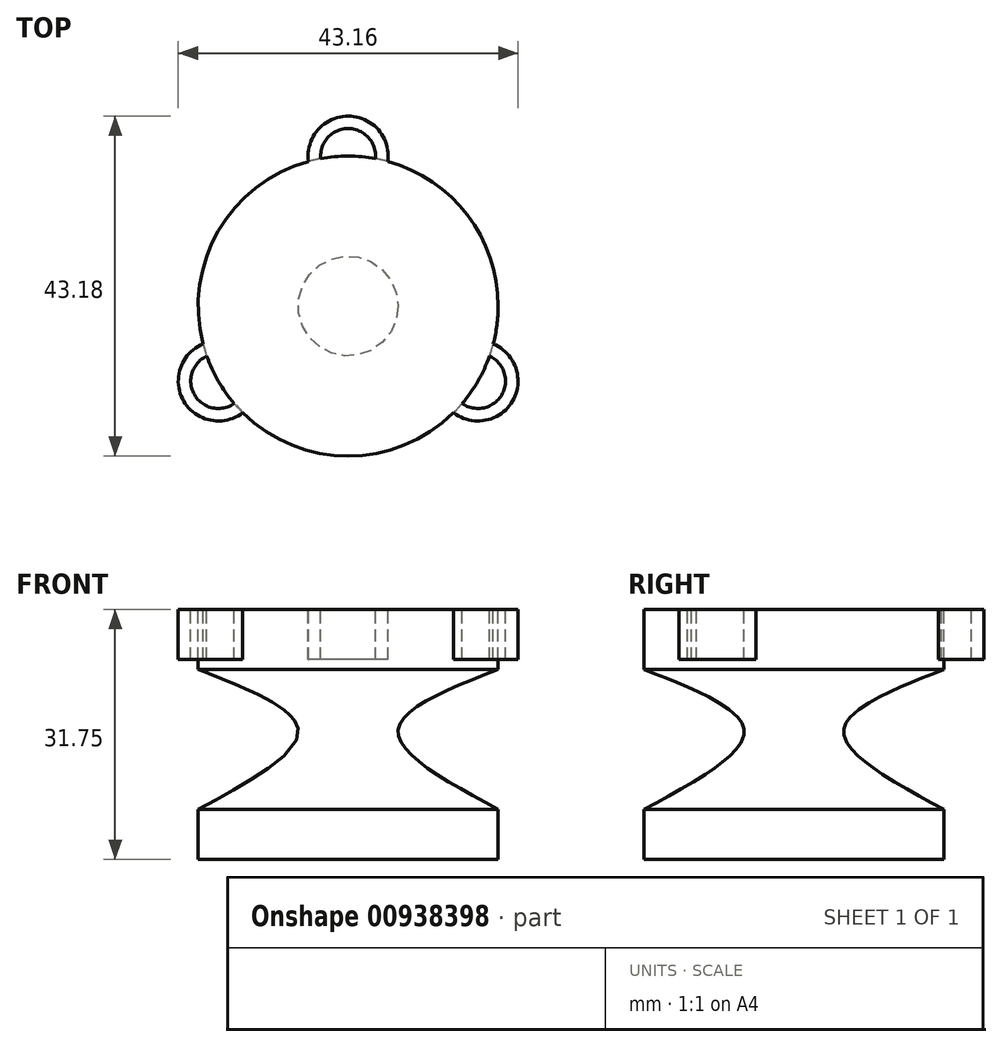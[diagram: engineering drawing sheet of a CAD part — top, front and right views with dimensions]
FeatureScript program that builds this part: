
annotation { "Feature Type Name" : "Feature", "Feature Type Description" : "" }
export const myFeature = defineFeature(function(context is Context, id is Id, definition is map)
    precondition{}
    {
        {
            var Q0;
            Q0=qCreatedBy(makeId("Top.planeOp"),FACE);
            var sketch = newSketch(context, id + "F0", { "sketchPlane" : qUnion([Q0])});
            skCircle(sketch, "E0", {"center": v(0, 0) * mm, "radius": 19.05 * mm});
            skCircle(sketch, "E1", {"center": v(0, 19.05) * mm, "radius": 5.08 * mm});
            skCircle(sketch, "E2.1.0", {"center": v(-16.5, -9.52) * mm, "radius": 5.08 * mm});
            skCircle(sketch, "E2.2.0", {"center": v(16.5, -9.53) * mm, "radius": 5.08 * mm});
            skCircle(sketch, "E3", {"center": v(0, 19.05) * mm, "radius": 3.5 * mm});
            skCircle(sketch, "E4.1.0", {"center": v(-16.5, -9.52) * mm, "radius": 3.5 * mm});
            skCircle(sketch, "E4.2.0", {"center": v(16.5, -9.53) * mm, "radius": 3.5 * mm});
            skSolve(sketch);
        }
        {
            var Q0;
            {var subQ0=sQuery(id+"F0.wireOp",EDGE,"E1");var subQ1=sQuery(id+"F0.wireOp",EDGE,"E0");var subQ8=makeQuery(id+"F0.imprint","INTERSECT",VERTEX,{"disambiguationData":[OD(0.0)],"derivedFrom":[subQ1,subQ0]});Q0=makeQuery(id+"F0.imprint","IMPRINT",FACE,{"disambiguationData":[TD([[makeQuery(id+"F0.imprint","IMPRINT",EDGE,{"disambiguationData":[TD([[subQ8,-1.0]])],"derivedFrom":subQ1}),1.0]])]});}
            var Q1;
            {var subQ0=sQuery(id+"F0.wireOp",EDGE,"E2.1.0");var subQ1=sQuery(id+"F0.wireOp",EDGE,"E0");var subQ2=makeQuery(id+"F0.imprint","INTERSECT",VERTEX,{"disambiguationData":[OD(0.0)],"derivedFrom":[subQ1,subQ0]});Q1=makeQuery(id+"F0.imprint","IMPRINT",FACE,{"disambiguationData":[TD([[makeQuery(id+"F0.imprint","IMPRINT",EDGE,{"disambiguationData":[TD([[subQ2,-1.0]])],"derivedFrom":subQ1}),1.0]])]});}
            var Q2;
            {var subQ0=sQuery(id+"F0.wireOp",EDGE,"E2.2.0");var subQ1=sQuery(id+"F0.wireOp",EDGE,"E0");var subQ2=makeQuery(id+"F0.imprint","INTERSECT",VERTEX,{"disambiguationData":[OD(0.0)],"derivedFrom":[subQ1,subQ0]});Q2=makeQuery(id+"F0.imprint","IMPRINT",FACE,{"disambiguationData":[TD([[makeQuery(id+"F0.imprint","IMPRINT",EDGE,{"disambiguationData":[TD([[subQ2,-1.0]])],"derivedFrom":subQ1}),1.0]])]});}
            var Q3;
            {var subQ0=sQuery(id+"F0.wireOp",EDGE,"E1");var subQ1=sQuery(id+"F0.wireOp",EDGE,"E0");var subQ2=makeQuery(id+"F0.imprint","INTERSECT",VERTEX,{"disambiguationData":[OD(0.0)],"derivedFrom":[subQ1,subQ0]});Q3=makeQuery(id+"F0.imprint","IMPRINT",FACE,{"disambiguationData":[TD([[makeQuery(id+"F0.imprint","IMPRINT",EDGE,{"disambiguationData":[TD([[subQ2,1.0]])],"derivedFrom":subQ1}),1.0]])]});}
            var Q4;
            {var subQ0=sQuery(id+"F0.wireOp",EDGE,"E3");var subQ1=sQuery(id+"F0.wireOp",EDGE,"E0");var subQ2=makeQuery(id+"F0.imprint","INTERSECT",VERTEX,{"disambiguationData":[OD(0.0)],"derivedFrom":[subQ1,subQ0]});Q4=makeQuery(id+"F0.imprint","IMPRINT",FACE,{"disambiguationData":[TD([[makeQuery(id+"F0.imprint","IMPRINT",EDGE,{"disambiguationData":[TD([[subQ2,-1.0]])],"derivedFrom":subQ1}),1.0]])]});}
            var Q5;
            {var subQ0=sQuery(id+"F0.wireOp",EDGE,"E4.1.0");var subQ1=sQuery(id+"F0.wireOp",EDGE,"E0");var subQ2=makeQuery(id+"F0.imprint","INTERSECT",VERTEX,{"disambiguationData":[OD(0.0)],"derivedFrom":[subQ1,subQ0]});Q5=makeQuery(id+"F0.imprint","IMPRINT",FACE,{"disambiguationData":[TD([[makeQuery(id+"F0.imprint","IMPRINT",EDGE,{"disambiguationData":[TD([[subQ2,-1.0]])],"derivedFrom":subQ1}),1.0]])]});}
            var Q6;
            {var subQ0=sQuery(id+"F0.wireOp",EDGE,"E4.2.0");var subQ1=sQuery(id+"F0.wireOp",EDGE,"E0");var subQ2=makeQuery(id+"F0.imprint","INTERSECT",VERTEX,{"disambiguationData":[OD(0.0)],"derivedFrom":[subQ1,subQ0]});Q6=makeQuery(id+"F0.imprint","IMPRINT",FACE,{"disambiguationData":[TD([[makeQuery(id+"F0.imprint","IMPRINT",EDGE,{"disambiguationData":[TD([[subQ2,-1.0]])],"derivedFrom":subQ1}),1.0]])]});}
            extrude(context, id + "F1", {"entities" : qUnion([Q0, Q1, Q2, Q3, Q4, Q5, Q6]), "oppositeDirection" : true, "depth" : 7.62 * mm, "offsetDistance" : 25.4 * mm});
        }
        {
            var Q0;
            {var subQ0=sQuery(id+"F0.wireOp",EDGE,"E1");var subQ1=sQuery(id+"F0.wireOp",EDGE,"E0");var subQ2=makeQuery(id+"F0.imprint","INTERSECT",VERTEX,{"disambiguationData":[OD(0.0)],"derivedFrom":[subQ1,subQ0]});Q0=makeQuery(id+"F0.imprint","IMPRINT",FACE,{"disambiguationData":[TD([[makeQuery(id+"F0.imprint","IMPRINT",EDGE,{"disambiguationData":[TD([[subQ2,-1.0]])],"derivedFrom":subQ1}),-1.0]])]});}
            var Q1;
            {var subQ0=sQuery(id+"F0.wireOp",EDGE,"E2.1.0");var subQ1=sQuery(id+"F0.wireOp",EDGE,"E0");var subQ2=makeQuery(id+"F0.imprint","INTERSECT",VERTEX,{"disambiguationData":[OD(0.0)],"derivedFrom":[subQ1,subQ0]});Q1=makeQuery(id+"F0.imprint","IMPRINT",FACE,{"disambiguationData":[TD([[makeQuery(id+"F0.imprint","IMPRINT",EDGE,{"disambiguationData":[TD([[subQ2,-1.0]])],"derivedFrom":subQ1}),-1.0]])]});}
            var Q2;
            {var subQ0=sQuery(id+"F0.wireOp",EDGE,"E2.2.0");var subQ1=sQuery(id+"F0.wireOp",EDGE,"E0");var subQ2=makeQuery(id+"F0.imprint","INTERSECT",VERTEX,{"disambiguationData":[OD(0.0)],"derivedFrom":[subQ1,subQ0]});Q2=makeQuery(id+"F0.imprint","IMPRINT",FACE,{"disambiguationData":[TD([[makeQuery(id+"F0.imprint","IMPRINT",EDGE,{"disambiguationData":[TD([[subQ2,-1.0]])],"derivedFrom":subQ1}),-1.0]])]});}
            extrude(context, id + "F2", {"entities" : qUnion([Q0, Q1, Q2]), "operationType" : NewBodyOperationType.ADD, "oppositeDirection" : true, "depth" : 6.35 * mm, "offsetDistance" : 25.4 * mm});
        }
        {
            var Q0;
            Q0=makeQuery(id+"F1.opExtrude","CAP_FACE",FACE,{"disambiguationData":[OSD([sQuery(id+"F0.wireOp",EDGE,"E0")])],"isStart":false});
            var sketch = newSketch(context, id + "F3", { "sketchPlane" : qUnion([Q0])});
            skCircle(sketch, "E5", {"center": v(0, 0) * mm, "radius": 19.05 * mm});
            skSolve(sketch);
        }
        {
            var Q0;
            Q0=qCreatedBy(makeId("Top.planeOp"),FACE);
            cPlane(context, id + "F4", {"entities" : qUnion([Q0]), "cplaneType" : CPlaneType.OFFSET, "offset" : 25.4 * mm, "oppositeDirection" : true, "width" : 152.4 * mm, "height" : 152.4 * mm});
        }
        {
            var Q0;
            Q0=qCreatedBy(id+"F4.planeOp",FACE);
            var sketch = newSketch(context, id + "F5", { "sketchPlane" : qUnion([Q0])});
            skCircle(sketch, "E6", {"center": v(0, 0) * mm, "radius": 19.05 * mm});
            skSolve(sketch);
        }
        {
            var Q0;
            Q0=qCreatedBy(makeId("Top.planeOp"),FACE);
            cPlane(context, id + "F6", {"entities" : qUnion([Q0]), "cplaneType" : CPlaneType.OFFSET, "offset" : 15.24 * mm, "oppositeDirection" : true, "width" : 152.4 * mm, "height" : 152.4 * mm});
        }
        {
            var Q0;
            Q0=qCreatedBy(id+"F6.planeOp",FACE);
            var sketch = newSketch(context, id + "F7", { "sketchPlane" : qUnion([Q0])});
            skCircle(sketch, "E7", {"center": v(0, 0) * mm, "radius": 6.35 * mm});
            skSolve(sketch);
        }
        {
            var Q0;
            Q0 = qSketchRegion(id + "F3", true);
            var Q1;
            Q1 = qSketchRegion(id + "F7", true);
            var Q2;
            Q2 = qSketchRegion(id + "F5", true);
            loft(context, id + "F8", {"sheetProfilesArray" : [{ "sheetProfileEntities" : qUnion([Q0]) }, { "sheetProfileEntities" : qUnion([Q1]) }, { "sheetProfileEntities" : qUnion([Q2]) }]});
        }
        {
            var Q0;
            Q0 = qSketchRegion(id + "F5", true);
            extrude(context, id + "F9", {"entities" : qUnion([Q0]), "oppositeDirection" : true, "depth" : 6.35 * mm, "offsetDistance" : 25.4 * mm});
        }
    });
